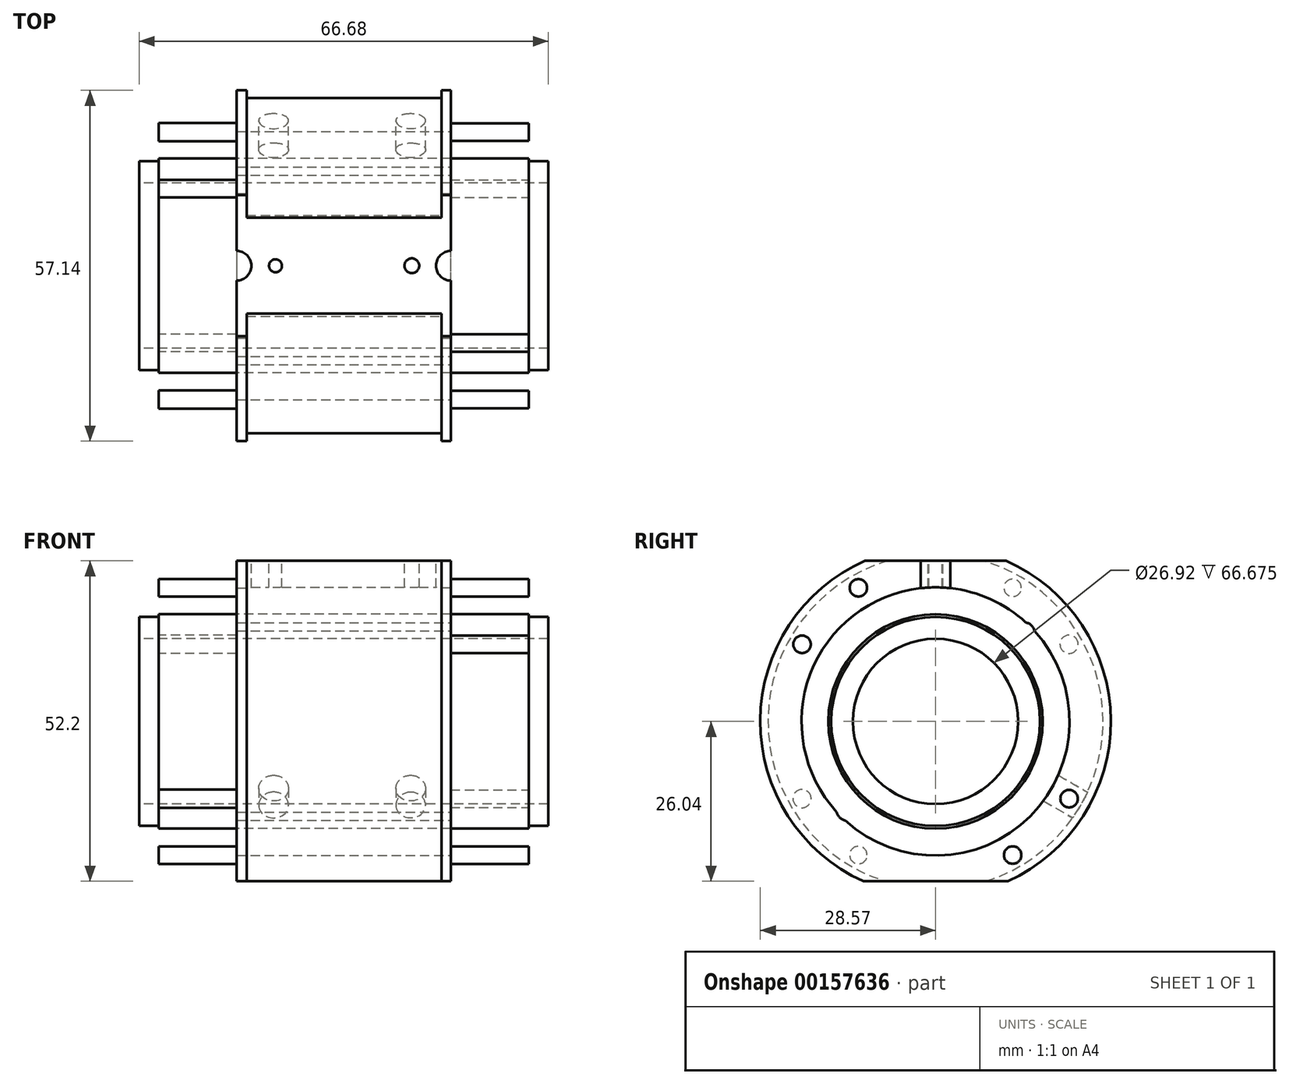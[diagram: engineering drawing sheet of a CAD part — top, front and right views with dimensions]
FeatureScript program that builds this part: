
annotation { "Feature Type Name" : "Feature", "Feature Type Description" : "" }
export const myFeature = defineFeature(function(context is Context, id is Id, definition is map)
    precondition{}
    {
        {
            var Q0;
            Q0=qCreatedBy(makeId("Right.planeOp"),FACE);
            var sketch = newSketch(context, id + "F0", { "sketchPlane" : qUnion([Q0])});
            skCircle(sketch, "E0", {"center": v(0, 0) * mm, "radius": 28.58 * mm});
            skCircle(sketch, "E1", {"center": v(0, 0) * mm, "radius": 13.46 * mm});
            skSolve(sketch);
        }
        {
            var Q0;
            Q0=makeQuery(id+"F0.imprint","IMPRINT",FACE,{"disambiguationData":[TD([[makeQuery(id+"F0.imprint","IMPRINT",EDGE,{"derivedFrom":sQuery(id+"F0.wireOp",EDGE,"E0")}),1.0]])]});
            extrude(context, id + "F1", {"entities" : qUnion([Q0]), "oppositeDirection" : true, "depth" : 14.22 * mm});
        }
        {
            var Q0;
            Q0=makeQuery(id+"F1.opExtrude","CAP_FACE",FACE,{"disambiguationData":[OSD([sQuery(id+"F0.wireOp",EDGE,"E0"),sQuery(id+"F0.wireOp",EDGE,"E1")])],"isStart":false});
            var sketch = newSketch(context, id + "F2", { "sketchPlane" : qUnion([Q0])});
            skCircle(sketch, "E2", {"center": v(0, 0) * mm, "radius": 27.3 * mm});
            skSolve(sketch);
        }
        {
            var Q0;
            Q0=makeQuery(id+"F2.imprint","IMPRINT",FACE,{"disambiguationData":[TD([[makeQuery(id+"F2.imprint","IMPRINT",EDGE,{"derivedFrom":sQuery(id+"F2.wireOp",EDGE,"E2")}),1.0]])]});
            extrude(context, id + "F3", {"entities" : qUnion([Q0]), "operationType" : NewBodyOperationType.ADD, "depth" : 31.75 * mm});
        }
        {
            var Q0;
            Q0=makeQuery(id+"F3.opExtrude","CAP_FACE",FACE,{"disambiguationData":[OSD([sQuery(id+"F0.wireOp",EDGE,"E1"),sQuery(id+"F2.wireOp",EDGE,"E2")])],"isStart":false});
            var sketch = newSketch(context, id + "F4", { "sketchPlane" : qUnion([Q0])});
            skCircle(sketch, "E3", {"center": v(0, 0) * mm, "radius": 28.58 * mm});
            skSolve(sketch);
        }
        {
            var Q0;
            Q0=makeQuery(id+"F4.imprint","IMPRINT",FACE,{"disambiguationData":[TD([[makeQuery(id+"F4.imprint","IMPRINT",EDGE,{"derivedFrom":sQuery(id+"F4.wireOp",EDGE,"E3")}),1.0]])]});
            var Q1;
            Q1=makeQuery(id+"F4.imprint","IMPRINT",FACE,{"disambiguationData":[TD([[makeQuery(id+"F4.imprint","IMPRINT",EDGE,{"derivedFrom":makeQuery(id+"F3.opExtrude","CAP_EDGE",EDGE,{"disambiguationData":[OSD([sQuery(id+"F2.wireOp",EDGE,"E2")])],"isStart":false})}),1.0]])]});
            extrude(context, id + "F5", {"entities" : qUnion([Q0, Q1]), "operationType" : NewBodyOperationType.ADD, "depth" : 14.35 * mm});
        }
        {
            var Q0;
            Q0=makeQuery(id+"F1.opExtrude","CAP_FACE",FACE,{"disambiguationData":[OSD([sQuery(id+"F0.wireOp",EDGE,"E0"),sQuery(id+"F0.wireOp",EDGE,"E1")])],"isStart":true});
            var sketch = newSketch(context, id + "F6", { "sketchPlane" : qUnion([Q0])});
            skLineSegment(sketch, "E4", {"start": v(0, 0) * mm, "end": v(0, 26.16) * mm});
            skLineSegment(sketch, "E5", {"start": v(0, 26.16) * mm, "end": v(-11.5, 26.16) * mm});
            skLineSegment(sketch, "E6", {"start": v(-11.5, 26.16) * mm, "end": v(11.5, 26.16) * mm});
            skSolve(sketch);
        }
        {
            var Q0;
            {var subQ0=sQuery(id+"F6.wireOp",EDGE,"E6");var subQ1=makeQuery(id+"F6.imprint","IMPRINT",VERTEX,{"derivedFrom":subQ0});Q0=makeQuery(id+"F6.imprint","IMPRINT",FACE,{"disambiguationData":[TD([[makeQuery(id+"F6.imprint","IMPRINT",EDGE,{"disambiguationData":[TD([[subQ1,1.0]])],"derivedFrom":subQ0}),1.0]])]});}
            extrude(context, id + "F7", {"entities" : qUnion([Q0]), "operationType" : NewBodyOperationType.REMOVE, "endBound" : BoundingType.THROUGH_ALL, "oppositeDirection" : true, "depth" : 25.4 * mm});
        }
        {
            var Q0;
            Q0=makeQuery(id+"F1.opExtrude","CAP_FACE",FACE,{"disambiguationData":[OSD([sQuery(id+"F0.wireOp",EDGE,"E0"),sQuery(id+"F0.wireOp",EDGE,"E1")])],"isStart":true});
            var sketch = newSketch(context, id + "F8", { "sketchPlane" : qUnion([Q0])});
            skCircle(sketch, "E7", {"center": v(0, 0) * mm, "radius": 21.84 * mm});
            skSolve(sketch);
        }
        {
            var Q0;
            Q0=makeQuery(id+"F8.imprint","IMPRINT",FACE,{"disambiguationData":[TD([[makeQuery(id+"F8.imprint","IMPRINT",EDGE,{"derivedFrom":sQuery(id+"F8.wireOp",EDGE,"E7")}),1.0]])]});
            extrude(context, id + "F9", {"entities" : qUnion([Q0]), "operationType" : NewBodyOperationType.REMOVE, "endBound" : BoundingType.THROUGH_ALL, "oppositeDirection" : true, "depth" : 25.4 * mm});
        }
        {
            var Q0;
            Q0=makeQuery(id+"F1.opExtrude","CAP_FACE",FACE,{"disambiguationData":[OSD([sQuery(id+"F0.wireOp",EDGE,"E0"),sQuery(id+"F0.wireOp",EDGE,"E1")])],"isStart":true});
            var sketch = newSketch(context, id + "F10", { "sketchPlane" : qUnion([Q0])});
            skCircle(sketch, "E8", {"center": v(0, 0) * mm, "radius": 17.46 * mm});
            skSolve(sketch);
        }
        {
            var Q0;
            Q0=makeQuery(id+"F10.imprint","IMPRINT",FACE,{"disambiguationData":[TD([[makeQuery(id+"F10.imprint","IMPRINT",EDGE,{"derivedFrom":sQuery(id+"F10.wireOp",EDGE,"E8")}),-1.0]])]});
            extrude(context, id + "F11", {"entities" : qUnion([Q0]), "operationType" : NewBodyOperationType.ADD, "oppositeDirection" : true, "depth" : 4.62 * mm});
        }
        {
            var Q0;
            Q0=makeQuery(id+"F5.opExtrude","CAP_FACE",FACE,{"disambiguationData":[OSD([sQuery(id+"F0.wireOp",EDGE,"E1"),sQuery(id+"F4.wireOp",EDGE,"E3")])],"isStart":false});
            var sketch = newSketch(context, id + "F12", { "sketchPlane" : qUnion([Q0])});
            skCircle(sketch, "E9", {"center": v(0, 0) * mm, "radius": 17.46 * mm});
            skSolve(sketch);
        }
        {
            var Q0;
            Q0=makeQuery(id+"F12.imprint","IMPRINT",FACE,{"disambiguationData":[TD([[makeQuery(id+"F12.imprint","IMPRINT",EDGE,{"derivedFrom":sQuery(id+"F12.wireOp",EDGE,"E9")}),-1.0]])]});
            extrude(context, id + "F13", {"entities" : qUnion([Q0]), "operationType" : NewBodyOperationType.ADD, "oppositeDirection" : true, "depth" : 4.62 * mm});
        }
        {
            var Q0;
            Q0=makeQuery(id+"F11.boolean.opBoolean","MERGE",FACE,{"derivedFrom":[makeQuery(id+"F1.opExtrude","CAP_FACE",FACE,{"disambiguationData":[OSD([sQuery(id+"F0.wireOp",EDGE,"E0"),sQuery(id+"F0.wireOp",EDGE,"E1")])],"isStart":true}),makeQuery(id+"F11.opExtrude","CAP_FACE",FACE,{"disambiguationData":[OSD([sQuery(id+"F8.wireOp",EDGE,"E7"),sQuery(id+"F10.wireOp",EDGE,"E8")])],"isStart":true})]});
            var sketch = newSketch(context, id + "F14", { "sketchPlane" : qUnion([Q0])});
            skCircle(sketch, "E10", {"center": v(0, 0) * mm, "radius": 13.46 * mm});
            skSolve(sketch);
        }
        {
            var Q0;
            Q0=makeQuery(id+"F14.imprint","IMPRINT",FACE,{"disambiguationData":[TD([[makeQuery(id+"F14.imprint","IMPRINT",EDGE,{"derivedFrom":sQuery(id+"F14.wireOp",EDGE,"E10")}),-1.0]])]});
            extrude(context, id + "F15", {"entities" : qUnion([Q0]), "operationType" : NewBodyOperationType.ADD, "depth" : 3.17 * mm, "hasSecondDirection" : true, "secondDirectionOppositeDirection" : true, "secondDirectionDepth" : 63.5 * mm});
        }
        {
            var Q0;
            Q0=makeQuery(id+"F11.boolean.opBoolean","MERGE",FACE,{"derivedFrom":[makeQuery(id+"F1.opExtrude","CAP_FACE",FACE,{"disambiguationData":[OSD([sQuery(id+"F0.wireOp",EDGE,"E0"),sQuery(id+"F0.wireOp",EDGE,"E1")])],"isStart":true}),makeQuery(id+"F11.opExtrude","CAP_FACE",FACE,{"disambiguationData":[OSD([sQuery(id+"F8.wireOp",EDGE,"E7"),sQuery(id+"F10.wireOp",EDGE,"E8")])],"isStart":true})]});
            var sketch = newSketch(context, id + "F16", { "sketchPlane" : qUnion([Q0])});
            skLineSegment(sketch, "E11", {"start": v(0, 0) * mm, "end": v(0, -26.03) * mm, "construction": true});
            skLineSegment(sketch, "E12", {"start": v(0, -26.03) * mm, "end": v(-11.78, -26.03) * mm});
            skLineSegment(sketch, "E13", {"start": v(-11.78, -26.03) * mm, "end": v(11.78, -26.03) * mm});
            skSolve(sketch);
        }
        {
            var Q0;
            {var subQ0=sQuery(id+"F16.wireOp",EDGE,"E13");var subQ3=makeQuery(id+"F16.imprint","IMPRINT",VERTEX,{"derivedFrom":subQ0});Q0=makeQuery(id+"F16.imprint","IMPRINT",FACE,{"disambiguationData":[TD([[makeQuery(id+"F16.imprint","IMPRINT",EDGE,{"disambiguationData":[TD([[subQ3,1.0]])],"derivedFrom":subQ0}),-1.0]])]});}
            extrude(context, id + "F17", {"entities" : qUnion([Q0]), "operationType" : NewBodyOperationType.REMOVE, "endBound" : BoundingType.THROUGH_ALL, "oppositeDirection" : true, "depth" : 25.4 * mm});
        }
        {
            var Q0;
            Q0=makeQuery(id+"F11.boolean.opBoolean","MERGE",FACE,{"derivedFrom":[makeQuery(id+"F1.opExtrude","CAP_FACE",FACE,{"disambiguationData":[OSD([sQuery(id+"F0.wireOp",EDGE,"E0"),sQuery(id+"F0.wireOp",EDGE,"E1")])],"isStart":true}),makeQuery(id+"F11.opExtrude","CAP_FACE",FACE,{"disambiguationData":[OSD([sQuery(id+"F8.wireOp",EDGE,"E7"),sQuery(id+"F10.wireOp",EDGE,"E8")])],"isStart":true})]});
            var sketch = newSketch(context, id + "F18", { "sketchPlane" : qUnion([Q0])});
            skCircle(sketch, "E14", {"center": v(12.57, 21.77) * mm, "radius": 1.42 * mm});
            skCircle(sketch, "E15", {"center": v(21.77, 12.57) * mm, "radius": 1.42 * mm});
            skCircle(sketch, "E16.MirrorC", {"center": v(-12.57, 21.77) * mm, "radius": 1.42 * mm});
            skCircle(sketch, "E17.MirrorC", {"center": v(-21.77, 12.57) * mm, "radius": 1.42 * mm});
            skCircle(sketch, "E18.MirrorC", {"center": v(-21.77, -12.57) * mm, "radius": 1.42 * mm});
            skCircle(sketch, "E19.MirrorC", {"center": v(-12.57, -21.77) * mm, "radius": 1.42 * mm});
            skCircle(sketch, "E20.MirrorC", {"center": v(12.57, -21.77) * mm, "radius": 1.42 * mm});
            skCircle(sketch, "E21.MirrorC", {"center": v(21.77, -12.57) * mm, "radius": 1.42 * mm});
            skSolve(sketch);
        }
        {
            var Q0;
            Q0=makeQuery(id+"F18.imprint","IMPRINT",FACE,{"disambiguationData":[TD([[makeQuery(id+"F18.imprint","IMPRINT",EDGE,{"derivedFrom":sQuery(id+"F18.wireOp",EDGE,"E16.MirrorC")}),-1.0]])]});
            var Q1;
            Q1=makeQuery(id+"F18.imprint","IMPRINT",FACE,{"disambiguationData":[TD([[makeQuery(id+"F18.imprint","IMPRINT",EDGE,{"derivedFrom":sQuery(id+"F18.wireOp",EDGE,"E17.MirrorC")}),-1.0]])]});
            var Q2;
            Q2=makeQuery(id+"F18.imprint","IMPRINT",FACE,{"disambiguationData":[TD([[makeQuery(id+"F18.imprint","IMPRINT",EDGE,{"derivedFrom":sQuery(id+"F18.wireOp",EDGE,"E18.MirrorC")}),1.0]])]});
            var Q3;
            Q3=makeQuery(id+"F18.imprint","IMPRINT",FACE,{"disambiguationData":[TD([[makeQuery(id+"F18.imprint","IMPRINT",EDGE,{"derivedFrom":sQuery(id+"F18.wireOp",EDGE,"E19.MirrorC")}),1.0]])]});
            var Q4;
            Q4=makeQuery(id+"F18.imprint","IMPRINT",FACE,{"disambiguationData":[TD([[makeQuery(id+"F18.imprint","IMPRINT",EDGE,{"derivedFrom":sQuery(id+"F18.wireOp",EDGE,"E20.MirrorC")}),-1.0]])]});
            var Q5;
            Q5=makeQuery(id+"F18.imprint","IMPRINT",FACE,{"disambiguationData":[TD([[makeQuery(id+"F18.imprint","IMPRINT",EDGE,{"derivedFrom":sQuery(id+"F18.wireOp",EDGE,"E21.MirrorC")}),-1.0]])]});
            var Q6;
            Q6=makeQuery(id+"F18.imprint","IMPRINT",FACE,{"disambiguationData":[TD([[makeQuery(id+"F18.imprint","IMPRINT",EDGE,{"derivedFrom":sQuery(id+"F18.wireOp",EDGE,"E15")}),1.0]])]});
            var Q7;
            Q7=makeQuery(id+"F18.imprint","IMPRINT",FACE,{"disambiguationData":[TD([[makeQuery(id+"F18.imprint","IMPRINT",EDGE,{"derivedFrom":sQuery(id+"F18.wireOp",EDGE,"E14")}),1.0]])]});
            extrude(context, id + "F19", {"entities" : qUnion([Q0, Q1, Q2, Q3, Q4, Q5, Q6, Q7]), "operationType" : NewBodyOperationType.REMOVE, "oppositeDirection" : true, "depth" : 12.7 * mm});
        }
        {
            var Q0;
            Q0=makeQuery(id+"F11.boolean.opBoolean","MERGE",FACE,{"derivedFrom":[makeQuery(id+"F1.opExtrude","CAP_FACE",FACE,{"disambiguationData":[OSD([sQuery(id+"F0.wireOp",EDGE,"E0"),sQuery(id+"F0.wireOp",EDGE,"E1")])],"isStart":true}),makeQuery(id+"F11.opExtrude","CAP_FACE",FACE,{"disambiguationData":[OSD([sQuery(id+"F8.wireOp",EDGE,"E7"),sQuery(id+"F10.wireOp",EDGE,"E8")])],"isStart":true})]});
            var sketch = newSketch(context, id + "F20", { "sketchPlane" : qUnion([Q0])});
            skCircle(sketch, "E22", {"center": v(14.38, 14.38) * mm, "radius": 1.78 * mm});
            skCircle(sketch, "E23.MirrorC", {"center": v(-14.38, 14.38) * mm, "radius": 1.78 * mm});
            skCircle(sketch, "E24.MirrorC", {"center": v(-14.38, -14.38) * mm, "radius": 1.78 * mm});
            skCircle(sketch, "E25.MirrorC", {"center": v(14.38, -14.38) * mm, "radius": 1.78 * mm});
            skSolve(sketch);
        }
        {
            var Q0;
            Q0=makeQuery(id+"F20.imprint","IMPRINT",FACE,{"disambiguationData":[TD([[makeQuery(id+"F20.imprint","IMPRINT",EDGE,{"derivedFrom":sQuery(id+"F20.wireOp",EDGE,"E23.MirrorC")}),-1.0]])]});
            var Q1;
            Q1=makeQuery(id+"F20.imprint","IMPRINT",FACE,{"disambiguationData":[TD([[makeQuery(id+"F20.imprint","IMPRINT",EDGE,{"derivedFrom":sQuery(id+"F20.wireOp",EDGE,"E22")}),1.0]])]});
            var Q2;
            Q2=makeQuery(id+"F20.imprint","IMPRINT",FACE,{"disambiguationData":[TD([[makeQuery(id+"F20.imprint","IMPRINT",EDGE,{"derivedFrom":sQuery(id+"F20.wireOp",EDGE,"E25.MirrorC")}),-1.0]])]});
            var Q3;
            Q3=makeQuery(id+"F20.imprint","IMPRINT",FACE,{"disambiguationData":[TD([[makeQuery(id+"F20.imprint","IMPRINT",EDGE,{"derivedFrom":sQuery(id+"F20.wireOp",EDGE,"E24.MirrorC")}),1.0]])]});
            extrude(context, id + "F21", {"entities" : qUnion([Q0, Q1, Q2, Q3]), "operationType" : NewBodyOperationType.REMOVE, "endBound" : BoundingType.THROUGH_ALL, "oppositeDirection" : true, "depth" : 25.4 * mm});
        }
        {
            var Q0;
            {var subQ0=sQuery(id+"F4.wireOp",EDGE,"E3");var subQ1=sQuery(id+"F0.wireOp",EDGE,"E1");Q0=makeQuery(id+"F13.boolean.opBoolean","MERGE",FACE,{"derivedFrom":[makeQuery(id+"F5.opExtrude","CAP_FACE",FACE,{"disambiguationData":[OSD([subQ1,subQ0])],"isStart":false}),makeQuery(id+"F13.opExtrude","CAP_FACE",FACE,{"disambiguationData":[OSD([subQ1,subQ0,sQuery(id+"F8.wireOp",EDGE,"E7"),sQuery(id+"F12.wireOp",EDGE,"E9")])],"isStart":true})]});}
            var sketch = newSketch(context, id + "F22", { "sketchPlane" : qUnion([Q0])});
            skCircle(sketch, "E26", {"center": v(12.57, 21.77) * mm, "radius": 1.42 * mm});
            skCircle(sketch, "E27", {"center": v(21.77, 12.57) * mm, "radius": 1.49 * mm});
            skCircle(sketch, "E28.MirrorC", {"center": v(-12.57, 21.77) * mm, "radius": 1.42 * mm});
            skCircle(sketch, "E29.MirrorC", {"center": v(-21.77, 12.57) * mm, "radius": 1.49 * mm});
            skCircle(sketch, "E30.MirrorC", {"center": v(-12.57, -21.77) * mm, "radius": 1.42 * mm});
            skCircle(sketch, "E31.MirrorC", {"center": v(-21.77, -12.57) * mm, "radius": 1.49 * mm});
            skCircle(sketch, "E32.MirrorC", {"center": v(12.57, -21.77) * mm, "radius": 1.42 * mm});
            skCircle(sketch, "E33.MirrorC", {"center": v(21.77, -12.57) * mm, "radius": 1.49 * mm});
            skSolve(sketch);
        }
        {
            var Q0;
            Q0=makeQuery(id+"F22.imprint","IMPRINT",FACE,{"disambiguationData":[TD([[makeQuery(id+"F22.imprint","IMPRINT",EDGE,{"derivedFrom":sQuery(id+"F22.wireOp",EDGE,"E28.MirrorC")}),-1.0]])]});
            var Q1;
            Q1=makeQuery(id+"F22.imprint","IMPRINT",FACE,{"disambiguationData":[TD([[makeQuery(id+"F22.imprint","IMPRINT",EDGE,{"derivedFrom":sQuery(id+"F22.wireOp",EDGE,"E29.MirrorC")}),-1.0]])]});
            var Q2;
            Q2=makeQuery(id+"F22.imprint","IMPRINT",FACE,{"disambiguationData":[TD([[makeQuery(id+"F22.imprint","IMPRINT",EDGE,{"derivedFrom":sQuery(id+"F22.wireOp",EDGE,"E31.MirrorC")}),1.0]])]});
            var Q3;
            Q3=makeQuery(id+"F22.imprint","IMPRINT",FACE,{"disambiguationData":[TD([[makeQuery(id+"F22.imprint","IMPRINT",EDGE,{"derivedFrom":sQuery(id+"F22.wireOp",EDGE,"E30.MirrorC")}),1.0]])]});
            var Q4;
            Q4=makeQuery(id+"F22.imprint","IMPRINT",FACE,{"disambiguationData":[TD([[makeQuery(id+"F22.imprint","IMPRINT",EDGE,{"derivedFrom":sQuery(id+"F22.wireOp",EDGE,"E32.MirrorC")}),-1.0]])]});
            var Q5;
            Q5=makeQuery(id+"F22.imprint","IMPRINT",FACE,{"disambiguationData":[TD([[makeQuery(id+"F22.imprint","IMPRINT",EDGE,{"derivedFrom":sQuery(id+"F22.wireOp",EDGE,"E33.MirrorC")}),-1.0]])]});
            var Q6;
            Q6=makeQuery(id+"F22.imprint","IMPRINT",FACE,{"disambiguationData":[TD([[makeQuery(id+"F22.imprint","IMPRINT",EDGE,{"derivedFrom":sQuery(id+"F22.wireOp",EDGE,"E27")}),1.0]])]});
            var Q7;
            Q7=makeQuery(id+"F22.imprint","IMPRINT",FACE,{"disambiguationData":[TD([[makeQuery(id+"F22.imprint","IMPRINT",EDGE,{"derivedFrom":sQuery(id+"F22.wireOp",EDGE,"E26")}),1.0]])]});
            extrude(context, id + "F23", {"entities" : qUnion([Q0, Q1, Q2, Q3, Q4, Q5, Q6, Q7]), "operationType" : NewBodyOperationType.REMOVE, "oppositeDirection" : true, "depth" : 12.7 * mm});
        }
        {
            var Q0;
            Q0=makeQuery(id+"F11.boolean.opBoolean","MERGE",FACE,{"derivedFrom":[makeQuery(id+"F1.opExtrude","CAP_FACE",FACE,{"disambiguationData":[OSD([sQuery(id+"F0.wireOp",EDGE,"E0"),sQuery(id+"F0.wireOp",EDGE,"E1")])],"isStart":true}),makeQuery(id+"F11.opExtrude","CAP_FACE",FACE,{"disambiguationData":[OSD([sQuery(id+"F8.wireOp",EDGE,"E7"),sQuery(id+"F10.wireOp",EDGE,"E8")])],"isStart":true})]});
            var sketch = newSketch(context, id + "F24", { "sketchPlane" : qUnion([Q0])});
            skLineSegment(sketch, "E34", {"start": v(0, 0) * mm, "end": v(21.77, -12.57) * mm, "construction": true});
            skLineSegment(sketch, "E35", {"start": v(21.77, -12.57) * mm, "end": v(24.74, -14.3) * mm});
            skSolve(sketch);
        }
        {
            var Q0;
            Q0=sQuery(id+"F24.wireOp",VERTEX,"E35.end");
            var Q1;
            Q1=sQuery(id+"F24.wireOp",EDGE,"E34");
            cPlane(context, id + "F25", {"entities" : qUnion([Q0, Q1]), "cplaneType" : CPlaneType.LINE_POINT, "offset" : 25.4 * mm, "width" : 152.4 * mm, "height" : 152.4 * mm});
        }
        {
            var Q0;
            Q0=qCreatedBy(id+"F25.planeOp",FACE);
            var sketch = newSketch(context, id + "F26", { "sketchPlane" : qUnion([Q0])});
            skLineSegment(sketch, "E36", {"start": v(0.19, 0) * mm, "end": v(49, 0) * mm, "construction": true});
            skCircle(sketch, "E37", {"center": v(19.24, 0) * mm, "radius": 2.41 * mm});
            skCircle(sketch, "E38", {"center": v(41.59, 0) * mm, "radius": 2.43 * mm});
            skSolve(sketch);
        }
        {
            var Q0;
            Q0=makeQuery(id+"F26.imprint","IMPRINT",FACE,{"disambiguationData":[TD([[makeQuery(id+"F26.imprint","IMPRINT",EDGE,{"derivedFrom":sQuery(id+"F26.wireOp",EDGE,"E37")}),1.0]])]});
            var Q1;
            Q1=makeQuery(id+"F26.imprint","IMPRINT",FACE,{"disambiguationData":[TD([[makeQuery(id+"F26.imprint","IMPRINT",EDGE,{"derivedFrom":sQuery(id+"F26.wireOp",EDGE,"E38")}),1.0]])]});
            extrude(context, id + "F27", {"entities" : qUnion([Q0, Q1]), "operationType" : NewBodyOperationType.REMOVE, "oppositeDirection" : true, "depth" : 10.16 * mm});
        }
        {
            var Q0;
            Q0=makeQuery(id+"F7.boolean.opBoolean","COPY",FACE,{"derivedFrom":makeQuery(id+"F7.opExtrude","SWEPT_FACE",FACE,{"disambiguationData":[OSD([sQuery(id+"F6.wireOp",EDGE,"E6")])]})});
            var sketch = newSketch(context, id + "F28", { "sketchPlane" : qUnion([Q0])});
            skCircle(sketch, "E39", {"center": v(-47.62, 0) * mm, "radius": 2.41 * mm});
            skPoint(sketch, "E39.centerSnap0", {"position": v(-60.33, 0) * mm});
            skCircle(sketch, "E40", {"center": v(-12.7, 0) * mm, "radius": 2.41 * mm});
            skSolve(sketch);
        }
        {
            var Q0;
            Q0=makeQuery(id+"F28.imprint","IMPRINT",FACE,{"disambiguationData":[TD([[makeQuery(id+"F28.imprint","IMPRINT",EDGE,{"derivedFrom":sQuery(id+"F28.wireOp",EDGE,"E39")}),1.0]])]});
            var Q1;
            Q1=makeQuery(id+"F28.imprint","IMPRINT",FACE,{"disambiguationData":[TD([[makeQuery(id+"F28.imprint","IMPRINT",EDGE,{"derivedFrom":sQuery(id+"F28.wireOp",EDGE,"E40")}),1.0]])]});
            extrude(context, id + "F29", {"entities" : qUnion([Q0, Q1]), "operationType" : NewBodyOperationType.REMOVE, "oppositeDirection" : true, "depth" : 6.35 * mm});
        }
        {
            var Q0;
            Q0=makeQuery(id+"F7.boolean.opBoolean","COPY",FACE,{"derivedFrom":makeQuery(id+"F7.opExtrude","SWEPT_FACE",FACE,{"disambiguationData":[OSD([sQuery(id+"F6.wireOp",EDGE,"E6")])]})});
            var sketch = newSketch(context, id + "F30", { "sketchPlane" : qUnion([Q0])});
            skCircle(sketch, "E41", {"center": v(-53.98, 0) * mm, "radius": 1.2 * mm});
            skCircle(sketch, "E42", {"center": v(-41.27, 0) * mm, "radius": 1.06 * mm});
            skCircle(sketch, "E43", {"center": v(-19.05, 0) * mm, "radius": 1.2 * mm});
            skCircle(sketch, "E44", {"center": v(-6.35, 0) * mm, "radius": 1.33 * mm});
            skLineSegment(sketch, "E45", {"start": v(-47.62, 0) * mm, "end": v(-47.62, 4.88) * mm, "construction": true});
            skLineSegment(sketch, "E46", {"start": v(-12.7, 0) * mm, "end": v(-12.7, 4.1) * mm, "construction": true});
            skSolve(sketch);
        }
        {
            var Q0;
            Q0=makeQuery(id+"F30.imprint","IMPRINT",FACE,{"disambiguationData":[TD([[makeQuery(id+"F30.imprint","IMPRINT",EDGE,{"derivedFrom":sQuery(id+"F30.wireOp",EDGE,"E41")}),1.0]])]});
            var Q1;
            Q1=makeQuery(id+"F30.imprint","IMPRINT",FACE,{"disambiguationData":[TD([[makeQuery(id+"F30.imprint","IMPRINT",EDGE,{"derivedFrom":sQuery(id+"F30.wireOp",EDGE,"E42")}),1.0]])]});
            var Q2;
            Q2=makeQuery(id+"F30.imprint","IMPRINT",FACE,{"disambiguationData":[TD([[makeQuery(id+"F30.imprint","IMPRINT",EDGE,{"derivedFrom":sQuery(id+"F30.wireOp",EDGE,"E43")}),1.0]])]});
            var Q3;
            Q3=makeQuery(id+"F30.imprint","IMPRINT",FACE,{"disambiguationData":[TD([[makeQuery(id+"F30.imprint","IMPRINT",EDGE,{"derivedFrom":sQuery(id+"F30.wireOp",EDGE,"E44")}),1.0]])]});
            extrude(context, id + "F31", {"entities" : qUnion([Q0, Q1, Q2, Q3]), "operationType" : NewBodyOperationType.REMOVE, "oppositeDirection" : true, "depth" : 6.35 * mm});
        }
        {
            var Q0;
            Q0=makeQuery(id+"F17.boolean.opBoolean","COPY",FACE,{"derivedFrom":makeQuery(id+"F17.opExtrude","SWEPT_FACE",FACE,{"disambiguationData":[OSD([sQuery(id+"F16.wireOp",EDGE,"E13")])]})});
            var sketch = newSketch(context, id + "F32", { "sketchPlane" : qUnion([Q0])});
            skCircle(sketch, "E47", {"center": v(-7.11, 0) * mm, "radius": 2.08 * mm});
            skCircle(sketch, "E48", {"center": v(-53.09, 0) * mm, "radius": 2.08 * mm});
            skSolve(sketch);
        }
        {
            var Q0;
            Q0=makeQuery(id+"F32.imprint","IMPRINT",FACE,{"disambiguationData":[TD([[makeQuery(id+"F32.imprint","IMPRINT",EDGE,{"derivedFrom":sQuery(id+"F32.wireOp",EDGE,"E47")}),1.0]])]});
            var Q1;
            Q1=makeQuery(id+"F32.imprint","IMPRINT",FACE,{"disambiguationData":[TD([[makeQuery(id+"F32.imprint","IMPRINT",EDGE,{"derivedFrom":sQuery(id+"F32.wireOp",EDGE,"E48")}),1.0]])]});
            extrude(context, id + "F33", {"entities" : qUnion([Q0, Q1]), "operationType" : NewBodyOperationType.REMOVE, "oppositeDirection" : true, "depth" : 6.35 * mm});
        }
        {
            var Q0;
            Q0=makeQuery(id+"F15.opExtrude","CAP_FACE",FACE,{"disambiguationData":[OSD([sQuery(id+"F10.wireOp",EDGE,"E8"),sQuery(id+"F14.wireOp",EDGE,"E10")])],"isStart":false});
            var sketch = newSketch(context, id + "F34", { "sketchPlane" : qUnion([Q0])});
            skCircle(sketch, "E49", {"center": v(0, 0) * mm, "radius": 17.02 * mm});
            skSolve(sketch);
        }
        {
            var Q0;
            Q0=makeQuery(id+"F34.imprint","IMPRINT",FACE,{"disambiguationData":[TD([[makeQuery(id+"F34.imprint","IMPRINT",EDGE,{"derivedFrom":sQuery(id+"F34.wireOp",EDGE,"E49")}),-1.0]])]});
            extrude(context, id + "F35", {"entities" : qUnion([Q0]), "operationType" : NewBodyOperationType.REMOVE, "oppositeDirection" : true, "depth" : 3.17 * mm});
        }
        {
            var Q0;
            Q0=makeQuery(id+"F15.opExtrude","CAP_FACE",FACE,{"disambiguationData":[OSD([sQuery(id+"F10.wireOp",EDGE,"E8"),sQuery(id+"F14.wireOp",EDGE,"E10")])],"isStart":true});
            var sketch = newSketch(context, id + "F36", { "sketchPlane" : qUnion([Q0])});
            skCircle(sketch, "E50", {"center": v(0, 0) * mm, "radius": 17.02 * mm});
            skSolve(sketch);
        }
        {
            var Q0;
            Q0=makeQuery(id+"F36.imprint","IMPRINT",FACE,{"disambiguationData":[TD([[makeQuery(id+"F36.imprint","IMPRINT",EDGE,{"derivedFrom":sQuery(id+"F36.wireOp",EDGE,"E50")}),-1.0]])]});
            extrude(context, id + "F37", {"entities" : qUnion([Q0]), "operationType" : NewBodyOperationType.REMOVE, "oppositeDirection" : true, "depth" : 3.17 * mm});
        }
    });
